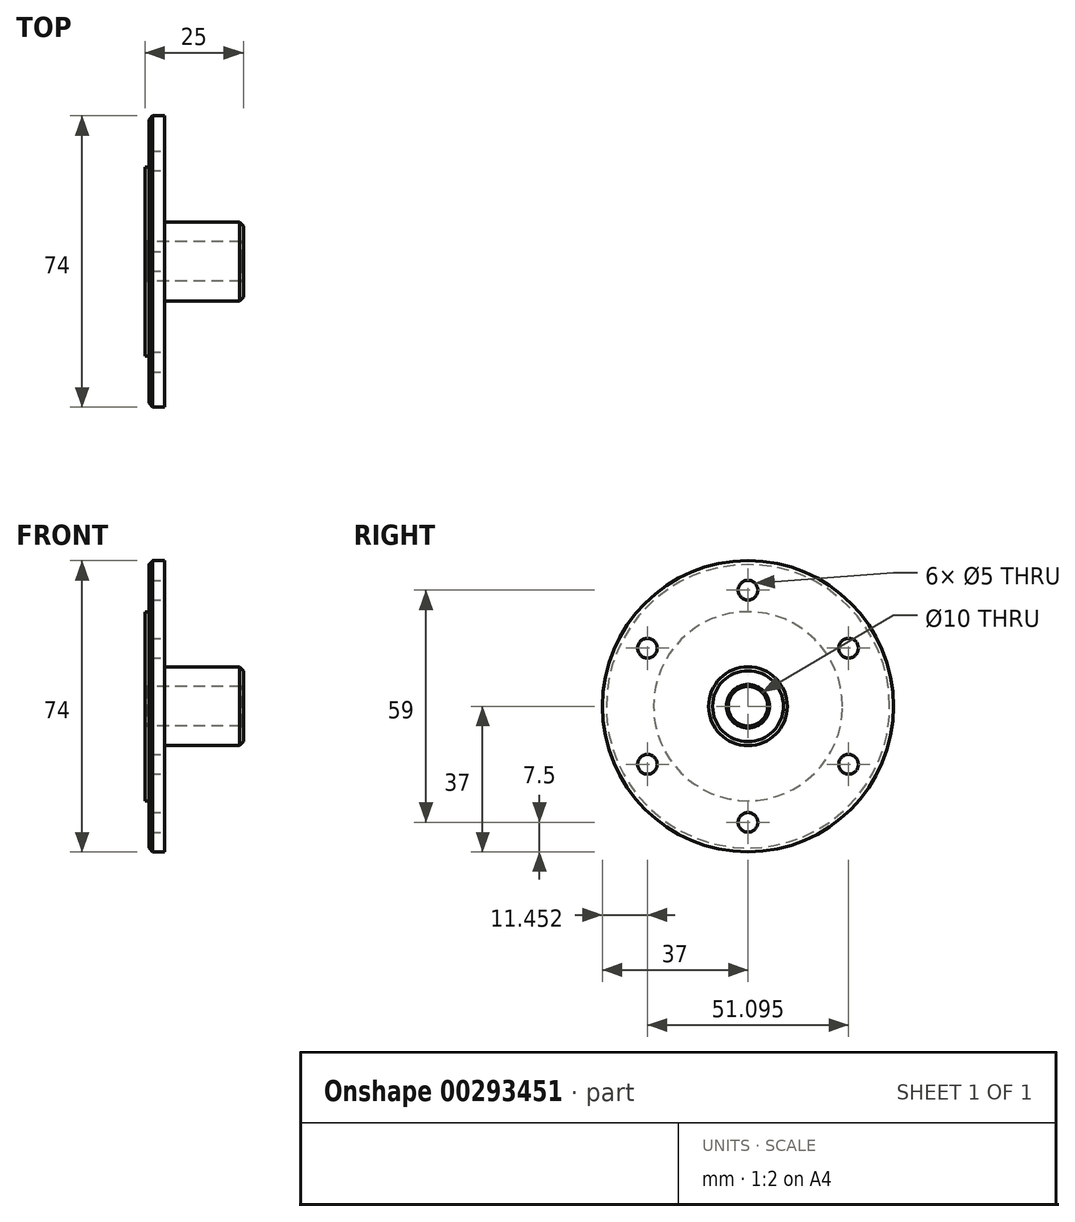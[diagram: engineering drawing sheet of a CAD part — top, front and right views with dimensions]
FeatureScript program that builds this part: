
annotation { "Feature Type Name" : "Feature", "Feature Type Description" : "" }
export const myFeature = defineFeature(function(context is Context, id is Id, definition is map)
    precondition{}
    {
        {
            var Q0;
            Q0=qCreatedBy(makeId("Front.planeOp"),FACE);
            var sketch = newSketch(context, id + "F0", { "sketchPlane" : qUnion([Q0])});
            skLineSegment(sketch, "E0", {"start": v(-26.84, 0) * mm, "end": v(30.3, 0) * mm, "construction": true});
            skLineSegment(sketch, "E1", {"start": v(-5, 5) * mm, "end": v(-5, 24) * mm});
            skLineSegment(sketch, "E2", {"start": v(-5, 24) * mm, "end": v(-4, 24) * mm});
            skLineSegment(sketch, "E3", {"start": v(-4, 24) * mm, "end": v(-4, 37) * mm});
            skLineSegment(sketch, "E4", {"start": v(-4, 37) * mm, "end": v(0, 37) * mm});
            skLineSegment(sketch, "E5", {"start": v(0, 37) * mm, "end": v(0, 10) * mm});
            skLineSegment(sketch, "E6", {"start": v(0, 10) * mm, "end": v(20, 10) * mm});
            skLineSegment(sketch, "E7", {"start": v(20, 10) * mm, "end": v(20, 5) * mm});
            skLineSegment(sketch, "E8", {"start": v(20, 5) * mm, "end": v(0, 5) * mm});
            skLineSegment(sketch, "E9", {"start": v(0, 5) * mm, "end": v(-5, 5) * mm});
            skSolve(sketch);
        }
        {
            var Q0;
            Q0=makeQuery(id+"F0.imprint","IMPRINT",FACE,{"disambiguationData":[TD([[makeQuery(id+"F0.imprint","IMPRINT",EDGE,{"derivedFrom":sQuery(id+"F0.wireOp",EDGE,"E1")}),-1.0]])]});
            var Q1;
            Q1=sQuery(id+"F0.wireOp",EDGE,"E0");
            revolve(context, id + "F1", {"entities" : qUnion([Q0]), "axis" : qUnion([Q1]), "revolveType" : RevolveType.FULL});
        }
        {
            var Q0;
            Q0=makeQuery(id+"F1.opRevolve","SWEPT_FACE",FACE,{"disambiguationData":[OSD([sQuery(id+"F0.wireOp",EDGE,"E5")])]});
            var sketch = newSketch(context, id + "F2", { "sketchPlane" : qUnion([Q0])});
            skCircle(sketch, "E10", {"center": v(0, 29.5) * mm, "radius": 2.5 * mm});
            skCircle(sketch, "E11.1.0", {"center": v(-25.55, 14.75) * mm, "radius": 2.5 * mm});
            skCircle(sketch, "E11.2.0", {"center": v(-25.55, -14.75) * mm, "radius": 2.5 * mm});
            skCircle(sketch, "E11.3.0", {"center": v(0, -29.5) * mm, "radius": 2.5 * mm});
            skCircle(sketch, "E11.4.0", {"center": v(25.55, -14.75) * mm, "radius": 2.5 * mm});
            skCircle(sketch, "E11.5.0", {"center": v(25.55, 14.75) * mm, "radius": 2.5 * mm});
            skPoint(sketch, "E11.center", {"position": v(0, 0) * mm});
            skLineSegment(sketch, "E12", {"start": v(-25.55, 14.75) * mm, "end": v(0, 0) * mm, "construction": true});
            skLineSegment(sketch, "E13.1.0", {"start": v(-25.55, -14.75) * mm, "end": v(0, 0) * mm, "construction": true});
            skLineSegment(sketch, "E13.2.0", {"start": v(0, -29.5) * mm, "end": v(0, 0) * mm, "construction": true});
            skLineSegment(sketch, "E13.3.0", {"start": v(25.55, -14.75) * mm, "end": v(0, 0) * mm, "construction": true});
            skLineSegment(sketch, "E13.4.0", {"start": v(25.55, 14.75) * mm, "end": v(0, 0) * mm, "construction": true});
            skLineSegment(sketch, "E13.5.0", {"start": v(0, 29.5) * mm, "end": v(0, 0) * mm, "construction": true});
            skSolve(sketch);
        }
        {
            var Q0;
            Q0=makeQuery(id+"F2.imprint","IMPRINT",FACE,{"disambiguationData":[TD([[makeQuery(id+"F2.imprint","IMPRINT",EDGE,{"derivedFrom":sQuery(id+"F2.wireOp",EDGE,"E10")}),1.0]])]});
            var Q1;
            Q1=makeQuery(id+"F2.imprint","IMPRINT",FACE,{"disambiguationData":[TD([[makeQuery(id+"F2.imprint","IMPRINT",EDGE,{"derivedFrom":sQuery(id+"F2.wireOp",EDGE,"E11.1.0")}),1.0]])]});
            var Q2;
            Q2=makeQuery(id+"F2.imprint","IMPRINT",FACE,{"disambiguationData":[TD([[makeQuery(id+"F2.imprint","IMPRINT",EDGE,{"derivedFrom":sQuery(id+"F2.wireOp",EDGE,"E11.2.0")}),1.0]])]});
            var Q3;
            Q3=makeQuery(id+"F2.imprint","IMPRINT",FACE,{"disambiguationData":[TD([[makeQuery(id+"F2.imprint","IMPRINT",EDGE,{"derivedFrom":sQuery(id+"F2.wireOp",EDGE,"E11.3.0")}),1.0]])]});
            var Q4;
            Q4=makeQuery(id+"F2.imprint","IMPRINT",FACE,{"disambiguationData":[TD([[makeQuery(id+"F2.imprint","IMPRINT",EDGE,{"derivedFrom":sQuery(id+"F2.wireOp",EDGE,"E11.4.0")}),1.0]])]});
            var Q5;
            Q5=makeQuery(id+"F2.imprint","IMPRINT",FACE,{"disambiguationData":[TD([[makeQuery(id+"F2.imprint","IMPRINT",EDGE,{"derivedFrom":sQuery(id+"F2.wireOp",EDGE,"E11.5.0")}),1.0]])]});
            extrude(context, id + "F3", {"entities" : qUnion([Q0, Q1, Q2, Q3, Q4, Q5]), "operationType" : NewBodyOperationType.REMOVE, "endBound" : BoundingType.THROUGH_ALL, "oppositeDirection" : true, "depth" : 25 * mm});
        }
        {
            var Q0;
            Q0=makeQuery(id+"F1.opRevolve","SWEPT_EDGE",EDGE,{"disambiguationData":[OSD([sQuery(id+"F0.wireOp",EDGE,"E6"),sQuery(id+"F0.wireOp",EDGE,"E7")])]});
            var Q1;
            Q1=makeQuery(id+"F1.opRevolve","SWEPT_EDGE",EDGE,{"disambiguationData":[OSD([sQuery(id+"F0.wireOp",EDGE,"E3"),sQuery(id+"F0.wireOp",EDGE,"E4")])]});
            chamfer(context, id + "F4", {"entities" : qUnion([Q0, Q1]), "width" : 1 * mm, "tangentPropagation" : true});
        }
        {
            var Q0;
            Q0=makeQuery(id+"F1.opRevolve","SWEPT_EDGE",EDGE,{"disambiguationData":[OSD([sQuery(id+"F0.wireOp",EDGE,"E1"),sQuery(id+"F0.wireOp",EDGE,"E9")])]});
            var Q1;
            Q1=makeQuery(id+"F1.opRevolve","SWEPT_EDGE",EDGE,{"disambiguationData":[OSD([sQuery(id+"F0.wireOp",EDGE,"E7"),sQuery(id+"F0.wireOp",EDGE,"E8")])]});
            chamfer(context, id + "F5", {"entities" : qUnion([Q0, Q1]), "width" : .5 * mm, "tangentPropagation" : true});
        }
    });
